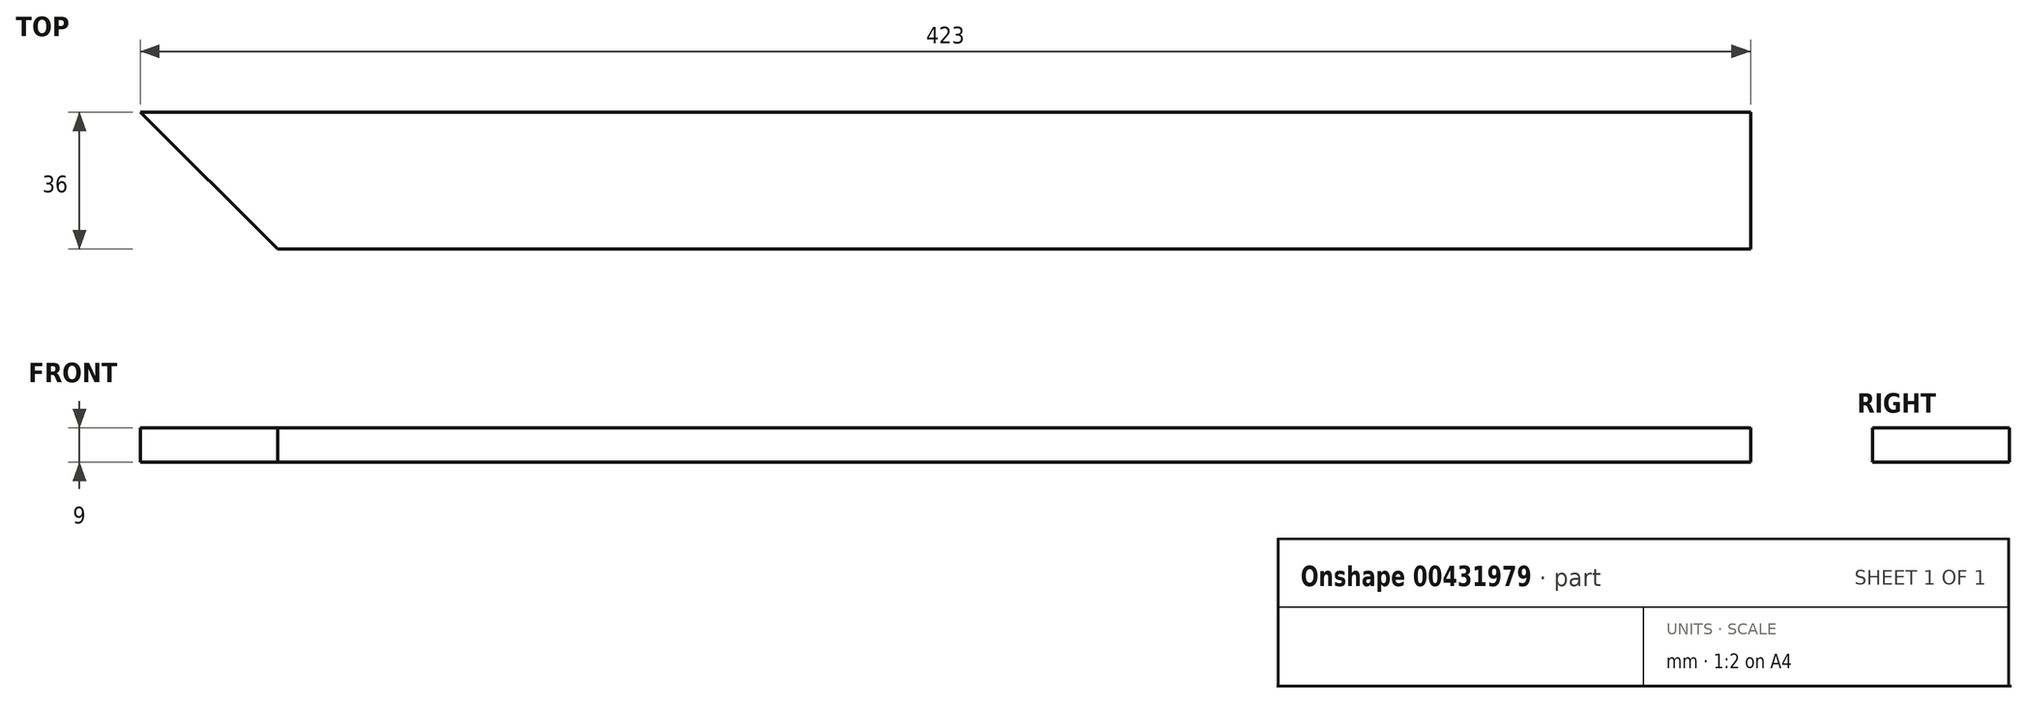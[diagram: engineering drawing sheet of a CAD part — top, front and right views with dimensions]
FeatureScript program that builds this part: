
annotation { "Feature Type Name" : "Feature", "Feature Type Description" : "" }
export const myFeature = defineFeature(function(context is Context, id is Id, definition is map)
    precondition{}
    {
        {
            var Q0;
            Q0=qCreatedBy(makeId("Top.planeOp"),FACE);
            var sketch = newSketch(context, id + "F0", { "sketchPlane" : qUnion([Q0])});
            skLineSegment(sketch, "E0.bottom", {"start": v(-211.5, 18) * mm, "end": v(211.5, 18) * mm});
            skLineSegment(sketch, "E0.top", {"start": v(-211.5, -18) * mm, "end": v(211.5, -18) * mm});
            skLineSegment(sketch, "E0.left", {"start": v(-211.5, 18) * mm, "end": v(-211.5, -18) * mm});
            skLineSegment(sketch, "E0.right", {"start": v(211.5, 18) * mm, "end": v(211.5, -18) * mm});
            skPoint(sketch, "E0.middle", {"position": v(0, 0) * mm});
            skSolve(sketch);
        }
        {
            var Q0;
            Q0=qSketchRegion(id+"F0",true);
            extrude(context, id + "F1", {"entities" : qUnion([Q0]), "depth" : 9 * mm, "offsetDistance" : 25 * mm});
        }
        {
            var Q0;
            Q0=makeQuery(id+"F1.opExtrude","SWEPT_EDGE",EDGE,{"disambiguationData":[OSD([sQuery(id+"F0.wireOp",EDGE,"E0.top"),sQuery(id+"F0.wireOp",EDGE,"E0.left")])]});
            chamfer(context, id + "F2", {"entities" : qUnion([Q0]), "width" : 36 * mm, "tangentPropagation" : true});
        }
    });
